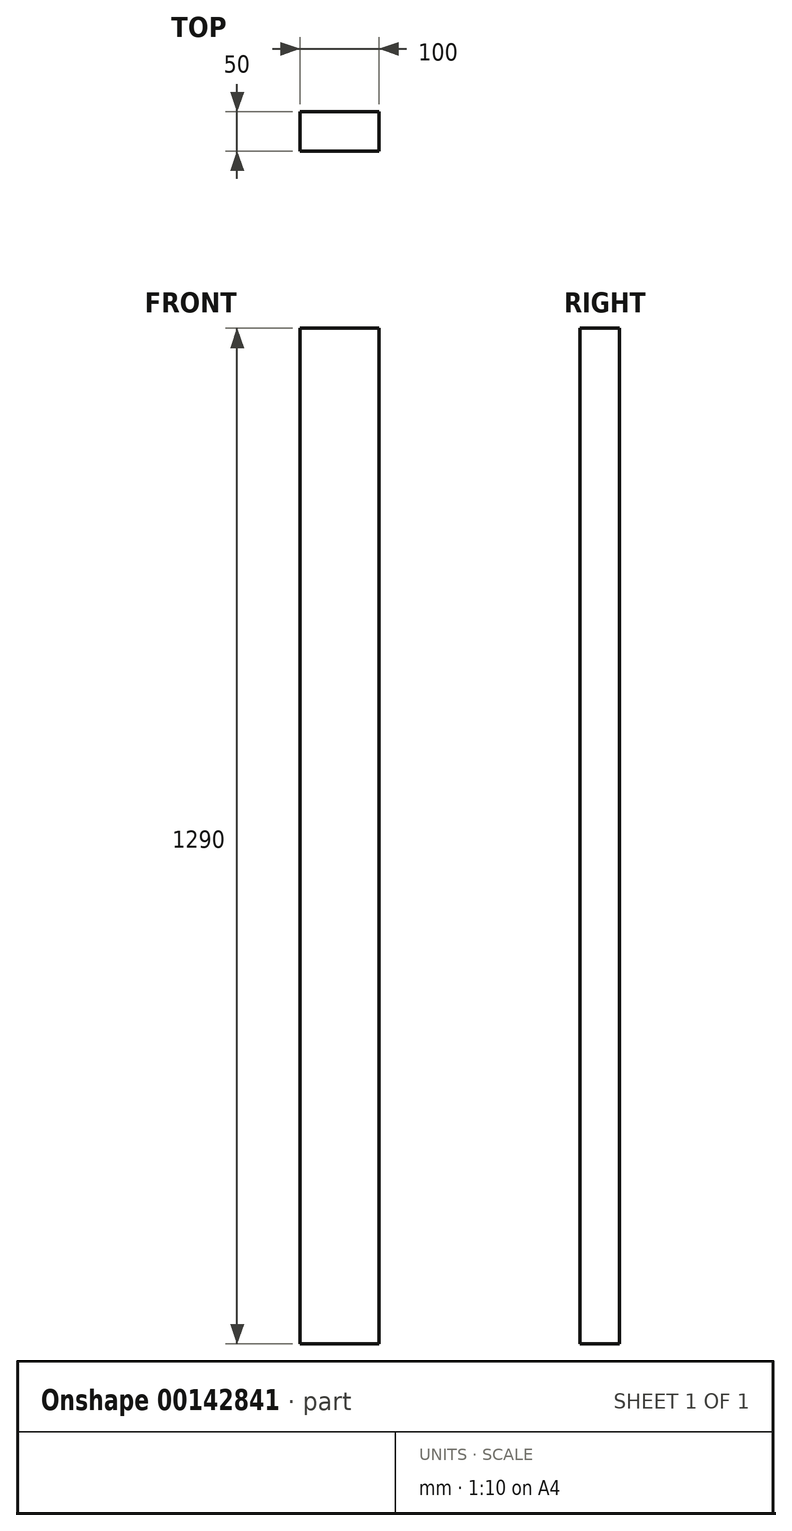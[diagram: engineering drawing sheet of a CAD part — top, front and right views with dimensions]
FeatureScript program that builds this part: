
annotation { "Feature Type Name" : "Feature", "Feature Type Description" : "" }
export const myFeature = defineFeature(function(context is Context, id is Id, definition is map)
    precondition{}
    {
        {
            var Q0;
            Q0=qCreatedBy(makeId("Front.planeOp"),FACE);
            var sketch = newSketch(context, id + "F0", { "sketchPlane" : qUnion([Q0])});
            skLineSegment(sketch, "E0.bottom", {"start": v(0, 0) * mm, "end": v(100, 0) * mm});
            skLineSegment(sketch, "E0.top", {"start": v(0, 1290) * mm, "end": v(100, 1290) * mm});
            skLineSegment(sketch, "E0.left", {"start": v(0, 0) * mm, "end": v(0, 1290) * mm});
            skLineSegment(sketch, "E0.right", {"start": v(100, 0) * mm, "end": v(100, 1290) * mm});
            skSolve(sketch);
        }
        {
            var Q0;
            Q0=qSketchRegion(id+"F0",true);
            extrude(context, id + "F1", {"entities" : qUnion([Q0]), "depth" : (50) * mm});
        }
    });
